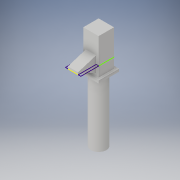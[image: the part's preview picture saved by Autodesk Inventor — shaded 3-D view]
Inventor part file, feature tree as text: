
AUTODESK INVENTOR PART (.ipt)
format: ipt  version: 2019 (Build 230136000, 136)  size: 229,888 bytes
history: native  units: in
note: dims shown in document units (in); Inventor stores cm internally (conversion verified against a paired STEP export)
features: extrude x12, sketch x10, fillet x3
ambient origin geometry x8: Origin, YZ Plane, XZ Plane, XY Plane, X Axis, Y Axis, Z Axis, Center Point
bodies: Solid1 (feature_tree)
feature tree (25):
  sketch  "Sketch1"  dims[d0=0.2362in d1=0.3937in d2=0.0in]
  extrude  "Extrusion1"  Depth=0.3937in TaperAngle=0.0deg
  extrude  "Extrusion2"  Depth=0.1181in
  extrude  "Extrusion3"  Depth=1.1811in
  extrude  "Extrusion4"  Depth=0.1575in
  fillet  "Fillet1"  Radius=0.3937in
  fillet  "Fillet2"  [1 undecoded]
  fillet  "Fillet3"  Radius=0.0197in
  extrude  "Extrusion5"  Depth=0.0394in
  sketch  "Sketch5"  dims[d15=0.0394in d16=0.0394in]
  extrude  "Extrusion6"  Depth=0.2362in
  extrude  "Extrusion7"  Depth=0.0394in
  extrude  "Extrusion8"  Depth=0.3937in TaperAngle=0.0deg
  sketch  "Sketch6"  dims[d17=0.3937in d18=0.0in d19=0.2362in]
  sketch  "Sketch7"  dims[d20=0.0394in d21=0.0394in]
  extrude  "Extrusion9"  Depth=0.1969in
  extrude  "Extrusion10"  Depth=0.1969in TaperAngle=0.0deg
  extrude  "Extrusion11"  Depth=0.0394in
  extrude  "Extrusion12"  Depth=0.0394in
  sketch  "Sketch2"  dims[d3=0.7874in d4=0.0in d5=0.1181in]
  sketch  "Sketch3"  dims[d6=0.2362in d7=1.1811in]
  sketch  "Sketch4"  dims[d8=0.2756in d9=0.0in d10=0.1575in d11=0.3937in d12=0.0in d13=0.0in d14=0.0197in]
  sketch  "Sketch9"  dims[d22=0.3937in d23=0.0in d24=0.3937in d25=0.0in]
  sketch  "Sketch10"  dims[d26=0.1969in d27=0.0in d28=0.0591in]
  sketch  "Sketch11"  dims[d29=0.1181in d30=0.0in d31=0.1969in d32=0.0in d33=0.0394in d34=0.0394in d35=0.0394in d36=0.0394in d37=0.0394in d38=0.0in d39=0.2362in d40=0.3937in d41=0.0in]
note: 1 required parameter value undecoded (feature->parameter linkage not recoverable at this tier; creation-order binding heuristic only, values carry confidence <= 0.55)
